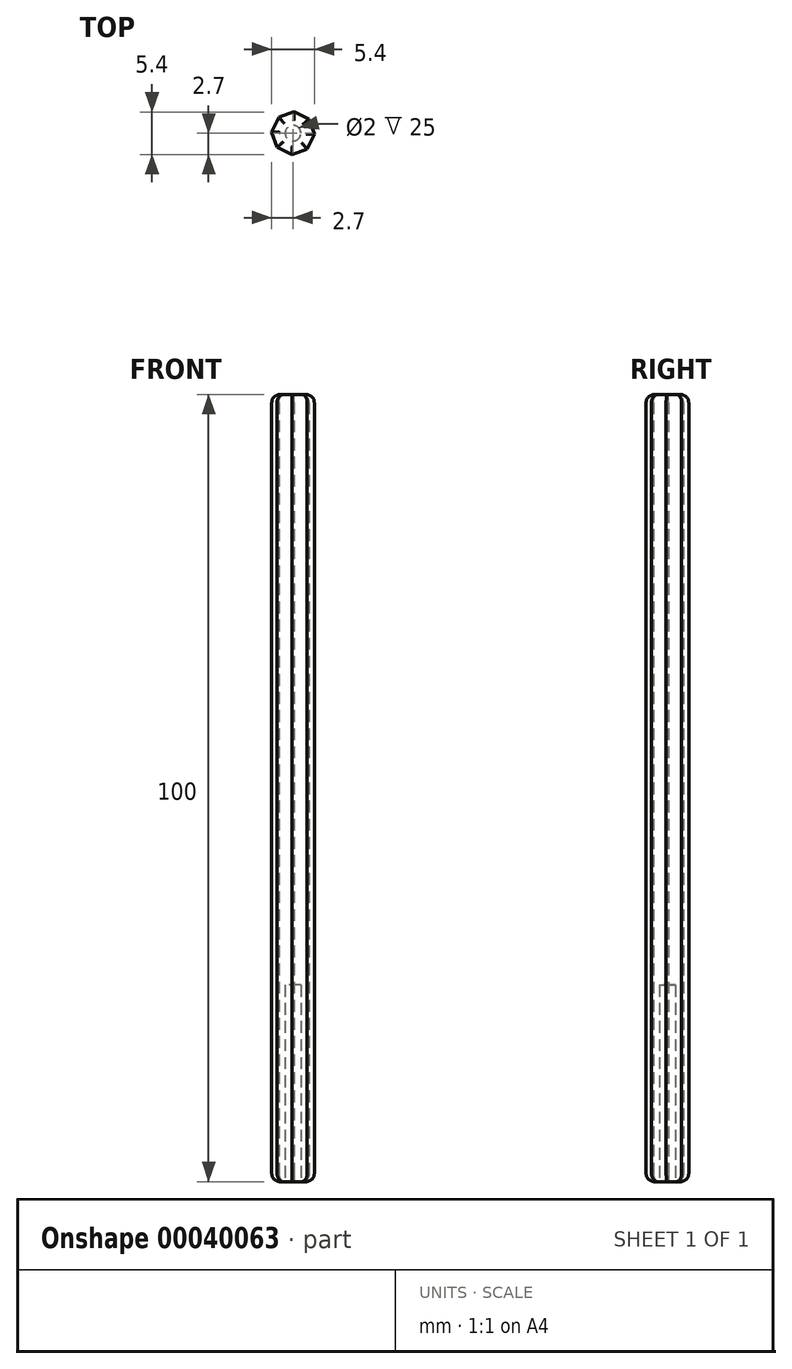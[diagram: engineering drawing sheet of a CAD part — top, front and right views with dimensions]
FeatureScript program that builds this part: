
annotation { "Feature Type Name" : "Feature", "Feature Type Description" : "" }
export const myFeature = defineFeature(function(context is Context, id is Id, definition is map)
    precondition{}
    {
        {
            var Q0;
            Q0=qCreatedBy(makeId("Top.planeOp"),FACE);
            var sketch = newSketch(context, id + "F0", { "sketchPlane" : qUnion([Q0])});
            skCircle(sketch, "E0.cCircle", {"center": v(0, 0) * mm, "radius": 2.7 * mm, "construction": true});
            skLineSegment(sketch, "E0.0", {"start": v(2.02, 1.8) * mm, "end": v(2.7, -0.16) * mm});
            skLineSegment(sketch, "E0.1", {"start": v(2.7, -0.16) * mm, "end": v(1.8, -2.02) * mm});
            skLineSegment(sketch, "E0.2", {"start": v(1.8, -2.02) * mm, "end": v(-0.16, -2.7) * mm});
            skLineSegment(sketch, "E0.3", {"start": v(-0.16, -2.7) * mm, "end": v(-2.02, -1.8) * mm});
            skLineSegment(sketch, "E0.4", {"start": v(-2.02, -1.8) * mm, "end": v(-2.7, 0.16) * mm});
            skLineSegment(sketch, "E0.5", {"start": v(-2.7, 0.16) * mm, "end": v(-1.8, 2.02) * mm});
            skLineSegment(sketch, "E0.6", {"start": v(-1.8, 2.02) * mm, "end": v(0.16, 2.7) * mm});
            skLineSegment(sketch, "E0.7", {"start": v(0.16, 2.7) * mm, "end": v(2.02, 1.8) * mm});
            skCircle(sketch, "E1", {"center": v(0, 0) * mm, "radius": 1 * mm});
            skSolve(sketch);
        }
        {
            var Q0;
            Q0=makeQuery(id+"F0.imprint","IMPRINT",FACE,{"disambiguationData":[TD([[makeQuery(id+"F0.imprint","IMPRINT",EDGE,{"derivedFrom":sQuery(id+"F0.wireOp",EDGE,"E0.0")}),-1.0]])]});
            var Q1;
            Q1=makeQuery(id+"F0.imprint","IMPRINT",FACE,{"disambiguationData":[TD([[makeQuery(id+"F0.imprint","IMPRINT",EDGE,{"derivedFrom":sQuery(id+"F0.wireOp",EDGE,"E1")}),1.0]])]});
            extrude(context, id + "F1", {"entities" : qUnion([Q0, Q1]), "depth" : 100 * mm});
        }
        {
            var Q0;
            Q0=makeQuery(id+"F1.opExtrude","CAP_FACE",FACE,{"disambiguationData":[OSD([sQuery(id+"F0.wireOp",EDGE,"E0.0"),sQuery(id+"F0.wireOp",EDGE,"E0.1"),sQuery(id+"F0.wireOp",EDGE,"E0.2"),sQuery(id+"F0.wireOp",EDGE,"E0.3"),sQuery(id+"F0.wireOp",EDGE,"E0.4"),sQuery(id+"F0.wireOp",EDGE,"E0.5"),sQuery(id+"F0.wireOp",EDGE,"E0.6"),sQuery(id+"F0.wireOp",EDGE,"E0.7")])],"isStart":true});
            var Q1;
            Q1=makeQuery(id+"F1.opExtrude","CAP_FACE",FACE,{"disambiguationData":[OSD([sQuery(id+"F0.wireOp",EDGE,"E0.0"),sQuery(id+"F0.wireOp",EDGE,"E0.1"),sQuery(id+"F0.wireOp",EDGE,"E0.2"),sQuery(id+"F0.wireOp",EDGE,"E0.3"),sQuery(id+"F0.wireOp",EDGE,"E0.4"),sQuery(id+"F0.wireOp",EDGE,"E0.5"),sQuery(id+"F0.wireOp",EDGE,"E0.6"),sQuery(id+"F0.wireOp",EDGE,"E0.7")])],"isStart":false});
            fillet(context, id + "F2", {"entities" : qUnion([Q0, Q1]), "radius" : 1 * mm, "tangentPropagation" : true, "allowEdgeOverflow" : false});
        }
        {
            var Q0;
            Q0=makeQuery(id+"F0.imprint","IMPRINT",FACE,{"disambiguationData":[TD([[makeQuery(id+"F0.imprint","IMPRINT",EDGE,{"derivedFrom":sQuery(id+"F0.wireOp",EDGE,"E1")}),1.0]])]});
            extrude(context, id + "F3", {"entities" : qUnion([Q0]), "operationType" : NewBodyOperationType.REMOVE, "depth" : 25 * mm});
        }
    });
